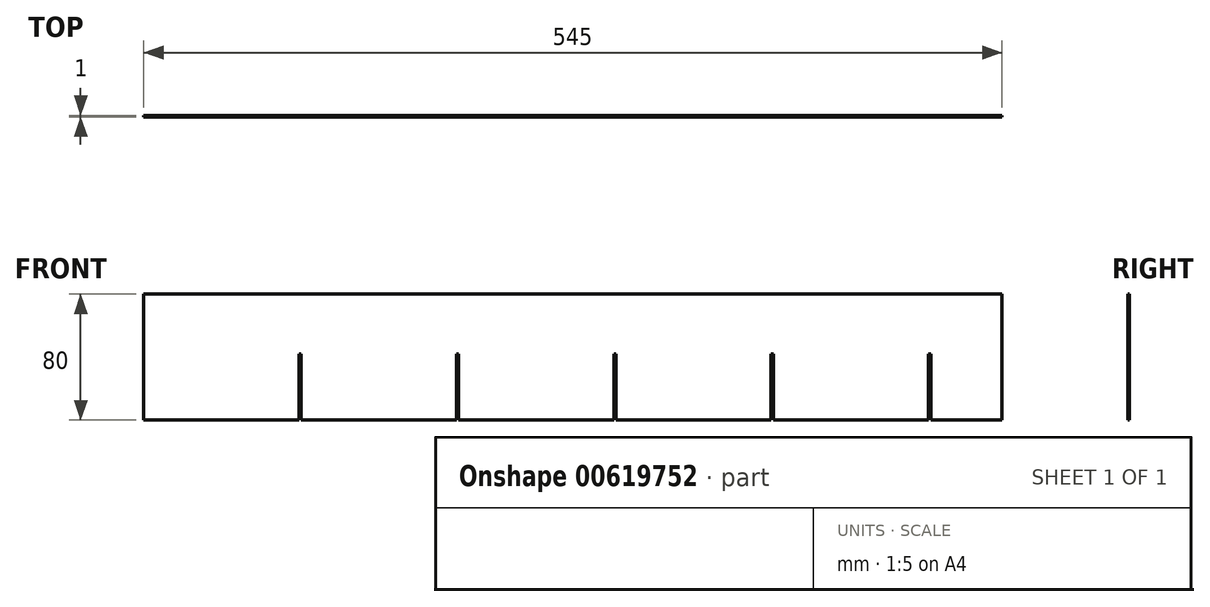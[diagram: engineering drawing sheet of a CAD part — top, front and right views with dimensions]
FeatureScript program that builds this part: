
annotation { "Feature Type Name" : "Feature", "Feature Type Description" : "" }
export const myFeature = defineFeature(function(context is Context, id is Id, definition is map)
    precondition{}
    {
        {
            var Q0;
            Q0=qCreatedBy(makeId("Front.planeOp"),FACE);
            var sketch = newSketch(context, id + "F0", { "sketchPlane" : qUnion([Q0])});
            skLineSegment(sketch, "E0", {"start": v(-67.02, -9.71) * mm, "end": v(31.48, -9.71) * mm});
            skLineSegment(sketch, "E1", {"start": v(31.48, -9.71) * mm, "end": v(31.48, 32.29) * mm});
            skLineSegment(sketch, "E2", {"start": v(31.48, 32.29) * mm, "end": v(32.98, 32.29) * mm});
            skLineSegment(sketch, "E3", {"start": v(32.98, 32.29) * mm, "end": v(32.98, -9.71) * mm});
            skLineSegment(sketch, "E4", {"start": v(32.98, -9.71) * mm, "end": v(131.48, -9.71) * mm});
            skLineSegment(sketch, "E5", {"start": v(131.48, -9.71) * mm, "end": v(131.48, 32.29) * mm});
            skLineSegment(sketch, "E6", {"start": v(131.48, 32.29) * mm, "end": v(132.98, 32.29) * mm});
            skLineSegment(sketch, "E7", {"start": v(132.98, 32.29) * mm, "end": v(132.98, -9.71) * mm});
            skLineSegment(sketch, "E8", {"start": v(132.98, -9.71) * mm, "end": v(231.48, -9.71) * mm});
            skLineSegment(sketch, "E9", {"start": v(231.48, -9.71) * mm, "end": v(231.48, 32.29) * mm});
            skLineSegment(sketch, "E10", {"start": v(231.48, 32.29) * mm, "end": v(232.98, 32.29) * mm});
            skLineSegment(sketch, "E11", {"start": v(232.98, 32.29) * mm, "end": v(232.98, -9.71) * mm});
            skLineSegment(sketch, "E12", {"start": v(232.98, -9.71) * mm, "end": v(331.48, -9.71) * mm});
            skLineSegment(sketch, "E13", {"start": v(331.48, -9.71) * mm, "end": v(331.48, 32.29) * mm});
            skLineSegment(sketch, "E14", {"start": v(331.48, 32.29) * mm, "end": v(332.98, 32.29) * mm});
            skLineSegment(sketch, "E15", {"start": v(332.98, 32.29) * mm, "end": v(332.98, -9.71) * mm});
            skLineSegment(sketch, "E16", {"start": v(332.98, -9.71) * mm, "end": v(431.48, -9.71) * mm});
            skLineSegment(sketch, "E17", {"start": v(431.48, -9.71) * mm, "end": v(431.48, 32.29) * mm});
            skLineSegment(sketch, "E18", {"start": v(431.48, 32.29) * mm, "end": v(432.98, 32.29) * mm});
            skLineSegment(sketch, "E19", {"start": v(432.98, 32.29) * mm, "end": v(432.98, -9.71) * mm});
            skLineSegment(sketch, "E20", {"start": v(-67.02, -9.71) * mm, "end": v(-67.02, 70.29) * mm});
            skLineSegment(sketch, "E21", {"start": v(-67.02, 70.29) * mm, "end": v(477.98, 70.29) * mm});
            skLineSegment(sketch, "E22", {"start": v(477.98, 70.29) * mm, "end": v(477.98, -9.71) * mm});
            skLineSegment(sketch, "E23", {"start": v(432.98, -9.71) * mm, "end": v(477.98, -9.71) * mm});
            skSolve(sketch);
        }
        {
            var Q0;
            Q0=makeQuery(id+"F0.imprint","IMPRINT",FACE,{"disambiguationData":[TD([[makeQuery(id+"F0.imprint","IMPRINT",EDGE,{"derivedFrom":sQuery(id+"F0.wireOp",EDGE,"E0")}),1.0]])]});
            extrude(context, id + "F1", {"entities" : qUnion([Q0]), "depth" : 1 * mm, "offsetDistance" : 25 * mm});
        }
    });
